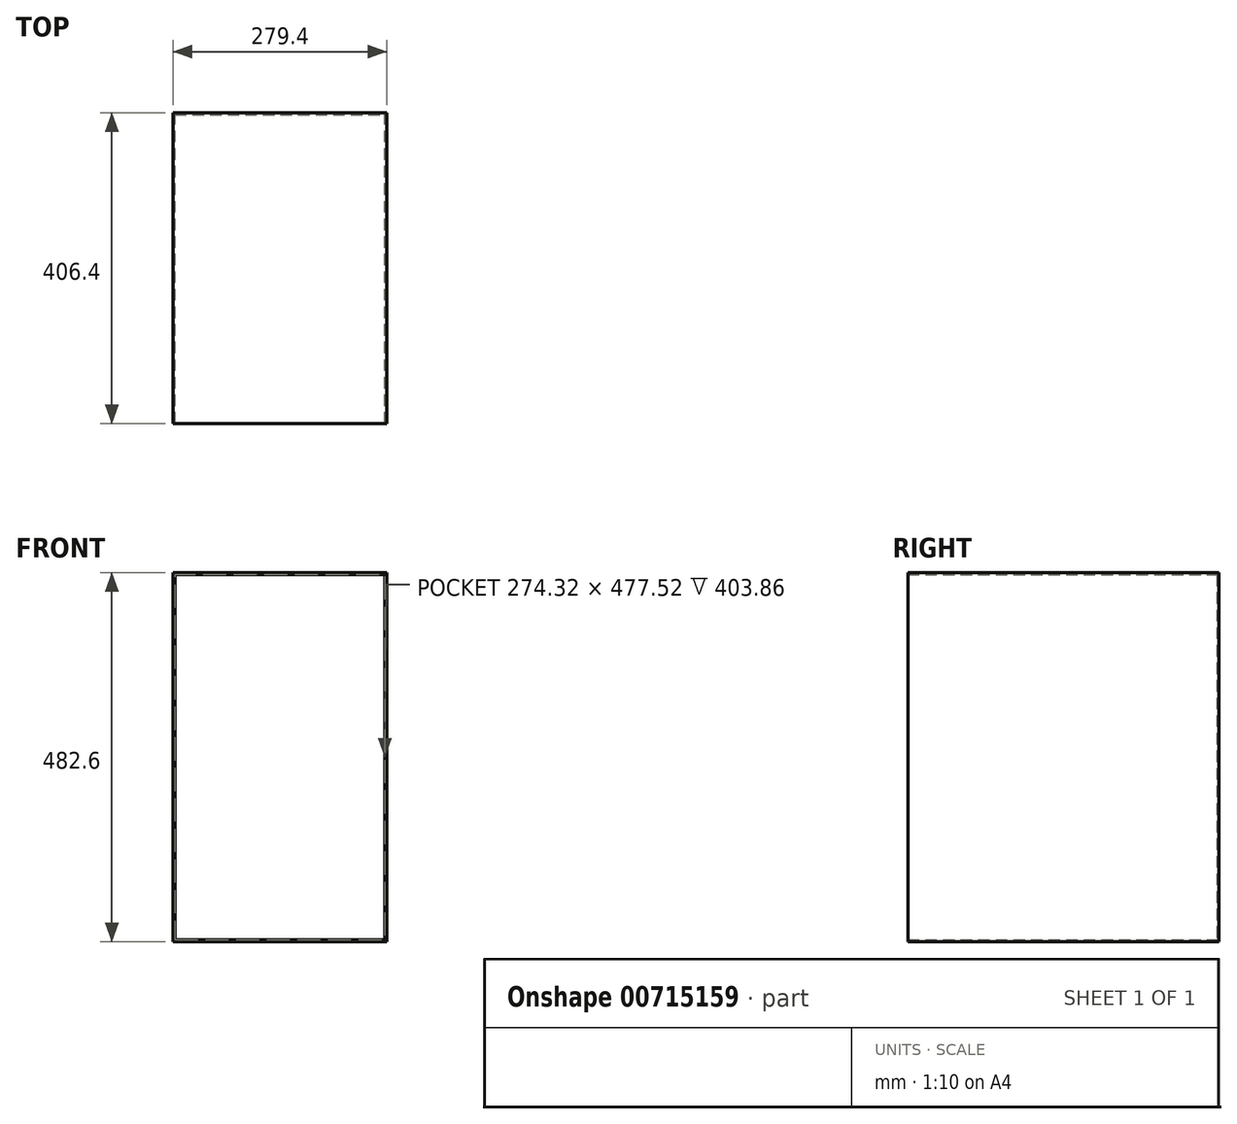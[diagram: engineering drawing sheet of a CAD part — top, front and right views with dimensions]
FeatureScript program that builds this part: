
annotation { "Feature Type Name" : "Feature", "Feature Type Description" : "" }
export const myFeature = defineFeature(function(context is Context, id is Id, definition is map)
    precondition{}
    {
        {
            var Q0;
            Q0=qCreatedBy(makeId("Front.planeOp"),FACE);
            var sketch = newSketch(context, id + "F0", { "sketchPlane" : qUnion([Q0])});
            skLineSegment(sketch, "E0.bottom", {"start": v(-255.8, 282.47) * mm, "end": v(23.6, 282.47) * mm});
            skLineSegment(sketch, "E0.top", {"start": v(-255.8, -200.13) * mm, "end": v(23.6, -200.13) * mm});
            skLineSegment(sketch, "E0.left", {"start": v(-255.8, 282.47) * mm, "end": v(-255.8, -200.13) * mm});
            skLineSegment(sketch, "E0.right", {"start": v(23.6, 282.47) * mm, "end": v(23.6, -200.13) * mm});
            skSolve(sketch);
        }
        {
            var Q0;
            Q0=makeQuery(id+"F0.imprint","IMPRINT",FACE,{"disambiguationData":[TD([[makeQuery(id+"F0.imprint","IMPRINT",EDGE,{"derivedFrom":sQuery(id+"F0.wireOp",EDGE,"E0.bottom")}),-1.0]])]});
            extrude(context, id + "F1", {"entities" : qUnion([Q0]), "depth" : 25.4 * mm, "offsetDistance" : 25.4 * mm});
        }
        {
            var Q0;
            Q0=qCreatedBy(makeId("Front.planeOp"),FACE);
            var sketch = newSketch(context, id + "F2", { "sketchPlane" : qUnion([Q0])});
            skSolve(sketch);
        }
        {
            var Q0;
            Q0=qSketchRegion(id+"F2",true);
            var Q1;
            Q1=makeQuery(id+"F1.opExtrude","CAP_FACE",FACE,{"disambiguationData":[OSD([sQuery(id+"F0.wireOp",EDGE,"E0.bottom"),sQuery(id+"F0.wireOp",EDGE,"E0.top"),sQuery(id+"F0.wireOp",EDGE,"E0.left"),sQuery(id+"F0.wireOp",EDGE,"E0.right")])],"isStart":false});
            extrude(context, id + "F3", {"entities" : qUnion([Q0, Q1]), "operationType" : NewBodyOperationType.ADD, "depth" : 381 * mm, "offsetDistance" : 25.4 * mm});
        }
        {
            var Q0;
            Q0=makeQuery(id+"F3.opExtrude","CAP_FACE",FACE,{"disambiguationData":[OSD([sQuery(id+"F0.wireOp",EDGE,"E0.bottom"),sQuery(id+"F0.wireOp",EDGE,"E0.top"),sQuery(id+"F0.wireOp",EDGE,"E0.left"),sQuery(id+"F0.wireOp",EDGE,"E0.right")])],"isStart":false});
            shell(context, id + "F4", {"entities" : qUnion([Q0]), "thickness" : 2.54 * mm});
        }
    });
